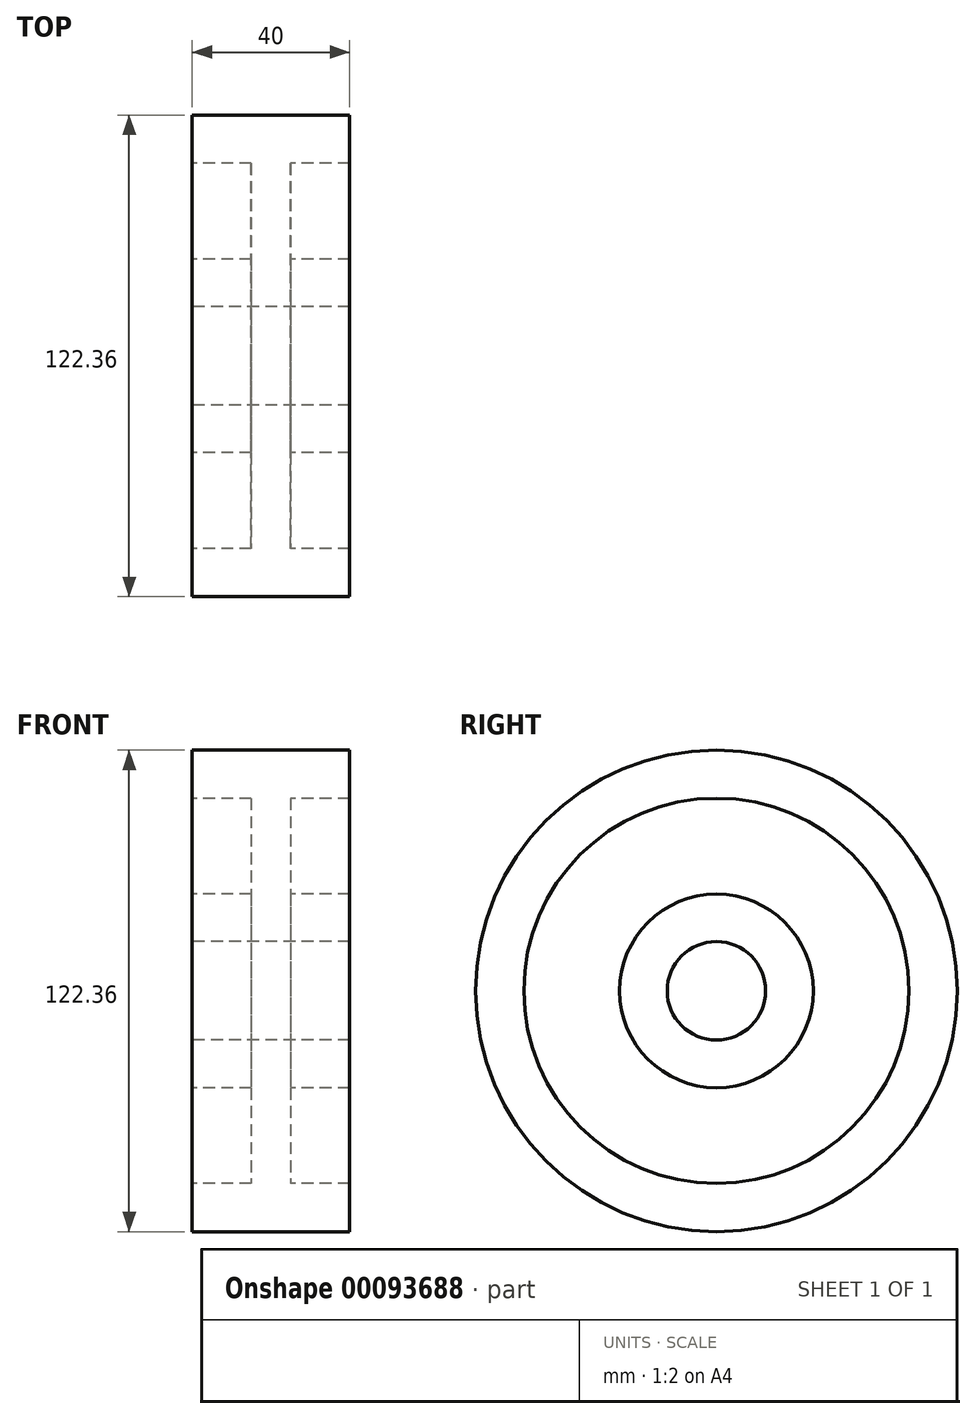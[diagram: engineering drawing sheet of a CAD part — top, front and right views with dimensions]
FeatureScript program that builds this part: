
annotation { "Feature Type Name" : "Feature", "Feature Type Description" : "" }
export const myFeature = defineFeature(function(context is Context, id is Id, definition is map)
    precondition{}
    {
        {
            var Q0;
            Q0=qCreatedBy(makeId("Front.planeOp"),FACE);
            var sketch = newSketch(context, id + "F0", { "sketchPlane" : qUnion([Q0])});
            skLineSegment(sketch, "E0", {"start": v(-41.34, 0) * mm, "end": v(33.78, 0) * mm, "construction": true});
            skLineSegment(sketch, "E1", {"start": v(-20, 12.5) * mm, "end": v(20, 12.5) * mm});
            skLineSegment(sketch, "E2", {"start": v(20, 24.6) * mm, "end": v(20, 12.5) * mm});
            skLineSegment(sketch, "E3", {"start": v(20, 24.6) * mm, "end": v(5, 24.6) * mm});
            skLineSegment(sketch, "E4", {"start": v(5, 24.6) * mm, "end": v(5, 48.94) * mm});
            skLineSegment(sketch, "E5", {"start": v(5, 48.94) * mm, "end": v(20, 48.94) * mm});
            skLineSegment(sketch, "E6", {"start": v(20, 48.94) * mm, "end": v(20, 61.18) * mm});
            skLineSegment(sketch, "E7", {"start": v(20, 61.18) * mm, "end": v(-20, 61.18) * mm});
            skLineSegment(sketch, "E8", {"start": v(-20, 61.18) * mm, "end": v(-20, 48.94) * mm});
            skLineSegment(sketch, "E9", {"start": v(-20, 48.94) * mm, "end": v(-5, 48.94) * mm});
            skLineSegment(sketch, "E10", {"start": v(-5, 48.94) * mm, "end": v(-5, 24.6) * mm});
            skLineSegment(sketch, "E11", {"start": v(-5, 24.6) * mm, "end": v(-20, 24.6) * mm});
            skLineSegment(sketch, "E12", {"start": v(-20, 24.6) * mm, "end": v(-20, 12.5) * mm});
            skLineSegment(sketch, "E13", {"start": v(0, 0) * mm, "end": v(0, 65.12) * mm, "construction": true});
            skSolve(sketch);
        }
        {
            var Q0;
            Q0 = qSketchRegion(id + "F0", true);
            var Q1;
            Q1=sQuery(id+"F0.wireOp",EDGE,"E0");
            revolve(context, id + "F1", {"entities" : qUnion([Q0]), "axis" : qUnion([Q1]), "revolveType" : RevolveType.FULL});
        }
    });
